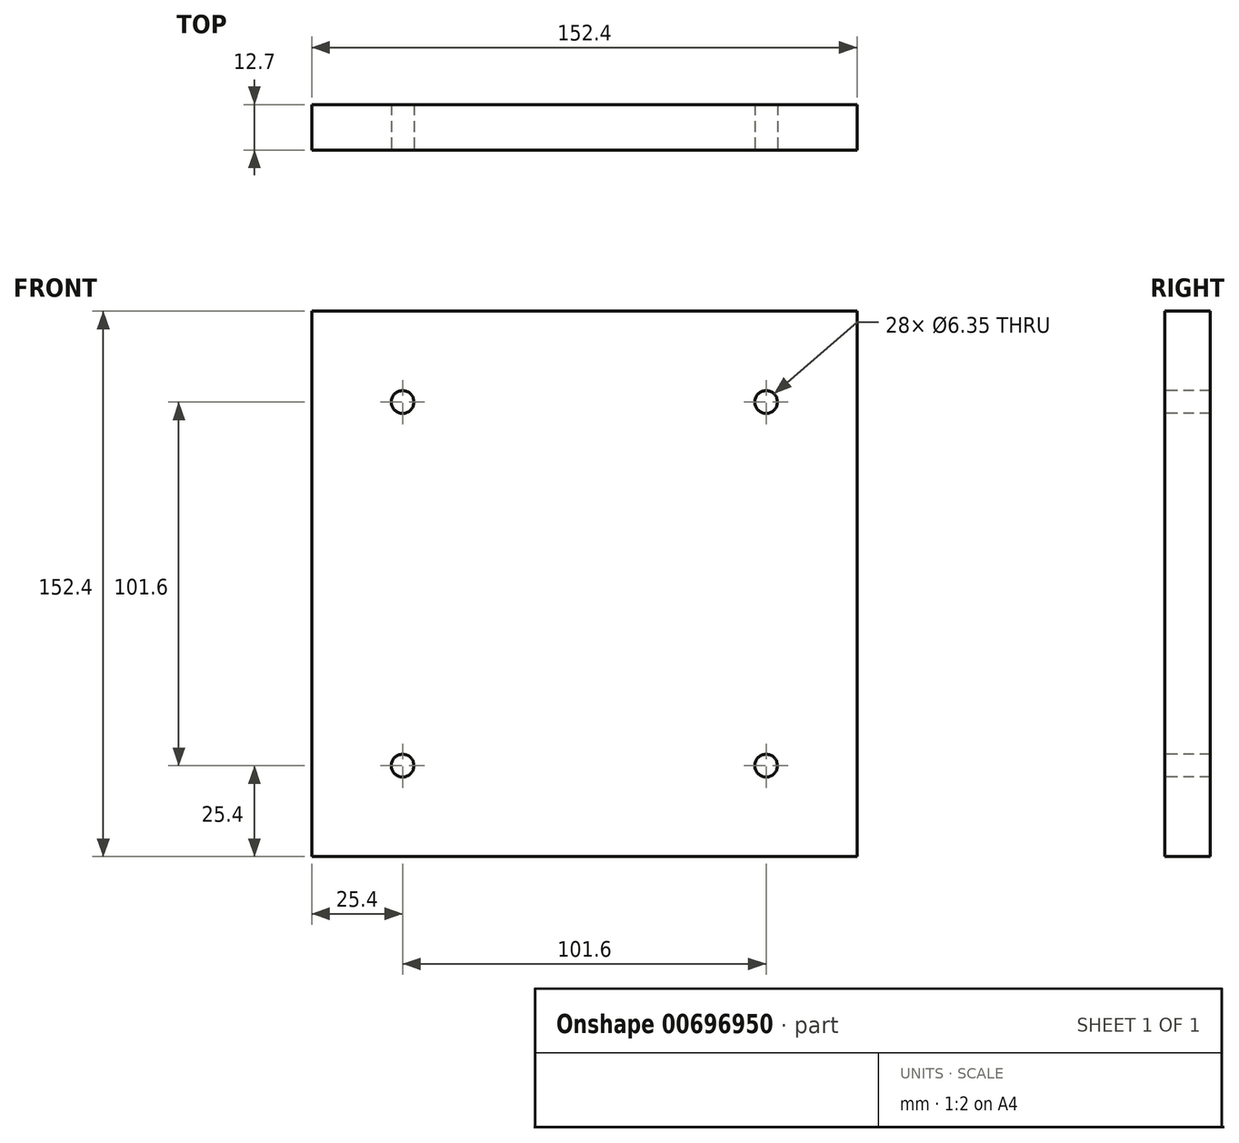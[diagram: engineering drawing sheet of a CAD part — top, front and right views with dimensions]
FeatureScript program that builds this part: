
annotation { "Feature Type Name" : "Feature", "Feature Type Description" : "" }
export const myFeature = defineFeature(function(context is Context, id is Id, definition is map)
    precondition{}
    {
        {
            var Q0;
            Q0=qCreatedBy(makeId("Front.planeOp"),FACE);
            var sketch = newSketch(context, id + "F0", { "sketchPlane" : qUnion([Q0])});
            skLineSegment(sketch, "E0.bottom", {"start": v(76.2, 76.2) * mm, "end": v(-76.2, 76.2) * mm});
            skLineSegment(sketch, "E0.top", {"start": v(76.2, -76.2) * mm, "end": v(-76.2, -76.2) * mm});
            skLineSegment(sketch, "E0.left", {"start": v(76.2, 76.2) * mm, "end": v(76.2, -76.2) * mm});
            skLineSegment(sketch, "E0.right", {"start": v(-76.2, 76.2) * mm, "end": v(-76.2, -76.2) * mm});
            skPoint(sketch, "E0.middle", {"position": v(0, 0) * mm});
            skSolve(sketch);
        }
        {
            var Q0;
            Q0 = qSketchRegion(id + "F0", true);
            extrude(context, id + "F1", {"entities" : qUnion([Q0]), "depth" : 12.7 * mm, "offsetDistance" : 25.4 * mm});
        }
        {
            var Q0;
            Q0=makeQuery(id+"F1.opExtrude","CAP_FACE",FACE,{"disambiguationData":[OSD([sQuery(id+"F0.wireOp",EDGE,"E0.bottom"),sQuery(id+"F0.wireOp",EDGE,"E0.top"),sQuery(id+"F0.wireOp",EDGE,"E0.left"),sQuery(id+"F0.wireOp",EDGE,"E0.right")])],"isStart":false});
            var sketch = newSketch(context, id + "F2", { "sketchPlane" : qUnion([Q0])});
            skLineSegment(sketch, "E1.bottom", {"start": v(50.8, 50.8) * mm, "end": v(-50.8, 50.8) * mm});
            skLineSegment(sketch, "E1.top", {"start": v(50.8, -50.8) * mm, "end": v(-50.8, -50.8) * mm});
            skLineSegment(sketch, "E1.left", {"start": v(50.8, 50.8) * mm, "end": v(50.8, -50.8) * mm});
            skLineSegment(sketch, "E1.right", {"start": v(-50.8, 50.8) * mm, "end": v(-50.8, -50.8) * mm});
            skPoint(sketch, "E1.middle", {"position": v(0, 0) * mm});
            skSolve(sketch);
        }
        {
            var Q0;
            Q0=sQuery(id+"F2.wireOp",VERTEX,"E1.right.start");
            var Q1;
            Q1=sQuery(id+"F2.wireOp",VERTEX,"E1.left.start");
            var Q2;
            Q2=sQuery(id+"F2.wireOp",VERTEX,"E1.top.start");
            var Q3;
            Q3=sQuery(id+"F2.wireOp",VERTEX,"E1.top.end");
            var Q4;
            Q4=makeQuery(id+"F1.opExtrude","SWEPT_BODY",BODY,{"disambiguationData":[OSD([sQuery(id+"F0.wireOp",EDGE,"E0.bottom"),sQuery(id+"F0.wireOp",EDGE,"E0.top"),sQuery(id+"F0.wireOp",EDGE,"E0.left"),sQuery(id+"F0.wireOp",EDGE,"E0.right")])]});
            hole(context, id + "F3", {"style" : HoleStyle.SIMPLE, "endStyle" : HoleEndStyle.THROUGH, "holeDiameter" : 6.35 * mm, "majorDiameter" : 6.35 * mm, "isTappedThrough" : true, "tappedDepth" : 12.7 * mm, "tapClearance" : 3, "startFromSketch" : true, "locations" : qUnion([Q0, Q1, Q2, Q3]), "scope" : qUnion([Q4])});
        }
    });
